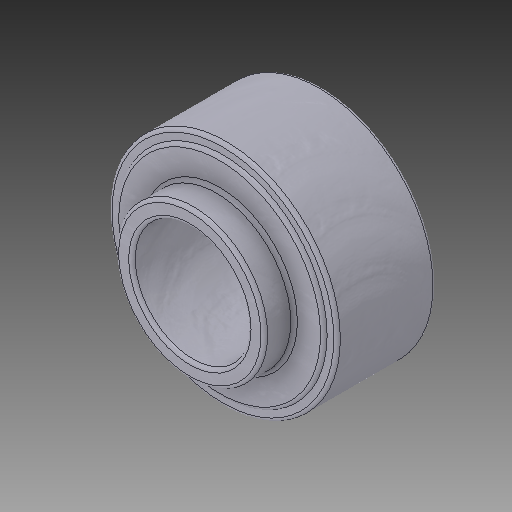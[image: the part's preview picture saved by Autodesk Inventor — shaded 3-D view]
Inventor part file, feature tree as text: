
AUTODESK INVENTOR PART (.ipt)
format: ipt  version: 2019 (Build 230136000, 136)  size: 232,448 bytes
history: native  units: mm
features: sketch x6, extrude x4, fillet x1
ambient origin geometry x8: Origin, YZ Plane, XZ Plane, XY Plane, X Axis, Y Axis, Z Axis, Center Point
bodies: Solid1 (feature_tree)
feature tree (11):
  sketch  "Sketch1"  dims[d0=69.0mm d1=30.0mm d2=0.0mm]
  sketch  "Sketch2"  dims[d3=63.0mm d4=1.0mm d5=0.0mm]
  extrude  "Extrusion1"  Depth=30.0mm TaperAngle=0.0deg
  extrude  "Extrusion2"  Depth=1.0mm TaperAngle=0.0deg
  extrude  "Extrusion3"  Depth=9.0mm TaperAngle=0.0deg
  extrude  "Extrusion4"  Depth=1.0mm TaperAngle=0.0deg
  fillet  "Fillet1"  Radius=1.0mm
  sketch  "Sketch6"
  sketch  "Sketch3"  dims[d6=45.0mm d7=9.0mm d8=0.0mm]
  sketch  "Sketch4"  dims[d9=35.0mm d10=110.0mm d11=0.0mm d12=1.0mm]
  sketch  "Sketch5"
